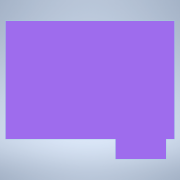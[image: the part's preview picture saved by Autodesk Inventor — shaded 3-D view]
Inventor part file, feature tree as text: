
AUTODESK INVENTOR PART (.ipt)
format: ipt  version: 2022 (Build 260153000, 153)  size: 122,368 bytes
history: native  units: mm
features: sketch x2, extrude x2
ambient origin geometry x8: Origin, YZ Plane, XZ Plane, XY Plane, X Axis, Y Axis, Z Axis, Center Point
bodies: Body1 (feature_tree)
feature tree (4):
  sketch  "Sketch2"  dims[d0=50.0mm d1=35.0mm]
  extrude  "Extrusion12"  Depth=35.0mm
  extrude  "Extrusion13"  Depth=15.0mm
  sketch  "Sketch7"  dims[d58=2.5mm d59=15.0mm d60=6.0mm d68=6.0mm d69=0.0mm d79=0.0mm d80=0.0mm d4=0.0mm d5=0.0mm d6=0.0mm d7=0.0mm]
